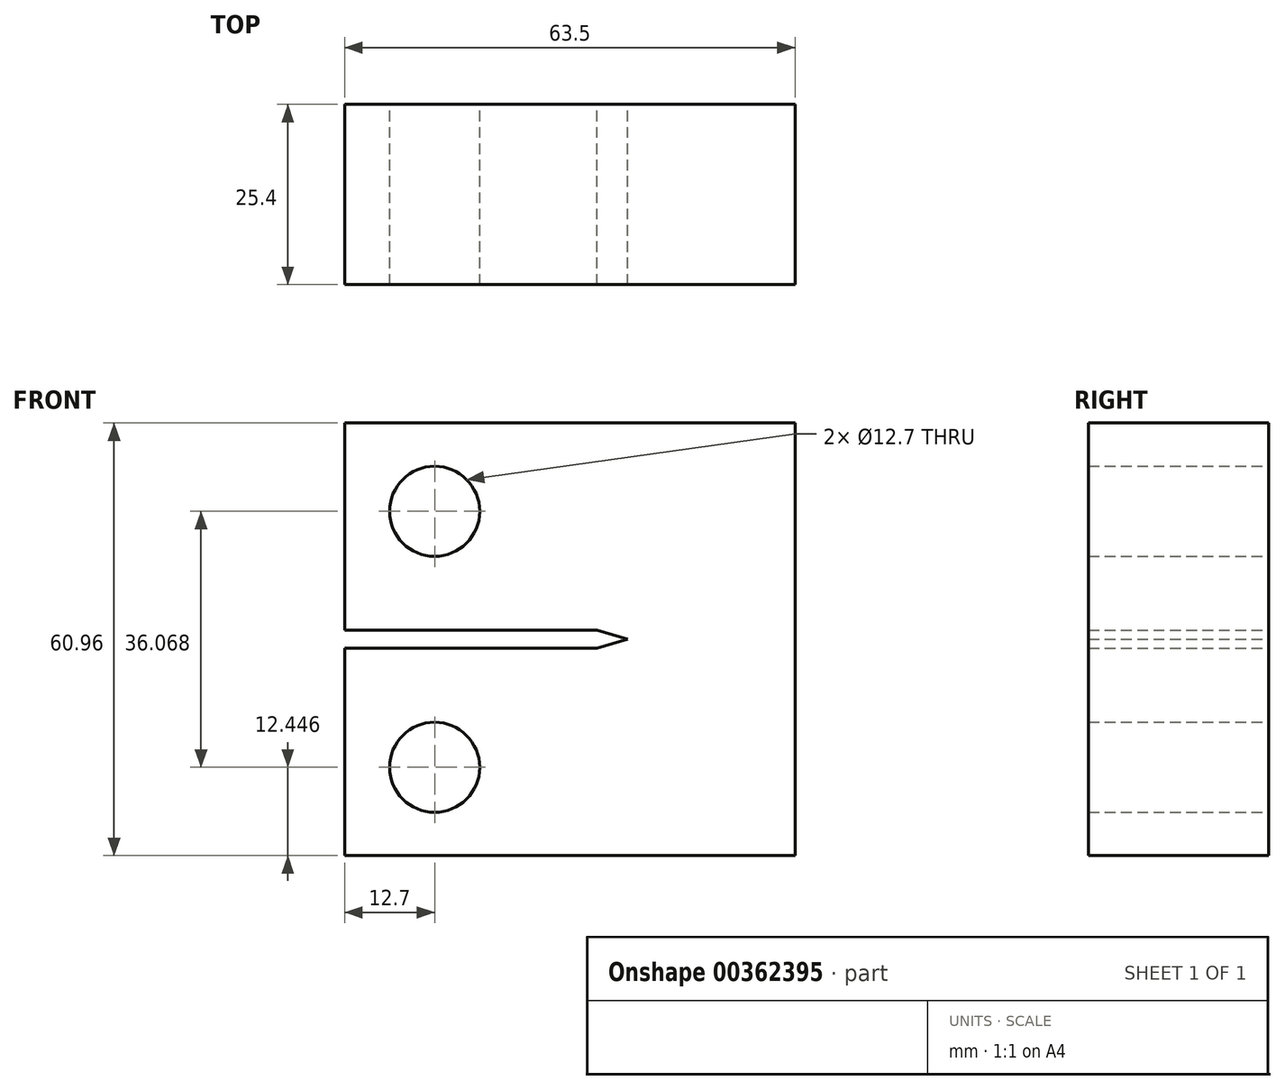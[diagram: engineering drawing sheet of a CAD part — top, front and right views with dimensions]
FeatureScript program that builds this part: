
annotation { "Feature Type Name" : "Feature", "Feature Type Description" : "" }
export const myFeature = defineFeature(function(context is Context, id is Id, definition is map)
    precondition{}
    {
        {
            var Q0;
            Q0=qCreatedBy(makeId("Front.planeOp"),FACE);
            var sketch = newSketch(context, id + "F0", { "sketchPlane" : qUnion([Q0])});
            skLineSegment(sketch, "E0.bottom", {"start": v(-31.75, -30.48) * mm, "end": v(31.75, -30.48) * mm});
            skLineSegment(sketch, "E0.top", {"start": v(-31.75, 30.48) * mm, "end": v(31.75, 30.48) * mm});
            skLineSegment(sketch, "E0.left", {"start": v(-31.75, -30.48) * mm, "end": v(-31.75, -1.27) * mm});
            skLineSegment(sketch, "E0.right", {"start": v(31.75, -30.48) * mm, "end": v(31.75, 30.48) * mm});
            skCircle(sketch, "E1", {"center": v(-19.05, 18.03) * mm, "radius": 6.35 * mm});
            skCircle(sketch, "E2", {"center": v(-19.05, -18.03) * mm, "radius": 6.35 * mm});
            skLineSegment(sketch, "E3.bottom", {"start": v(-31.75, -1.27) * mm, "end": v(3.81, -1.27) * mm});
            skLineSegment(sketch, "E3.top", {"start": v(-31.75, 1.27) * mm, "end": v(3.81, 1.27) * mm});
            skLineSegment(sketch, "E4", {"start": v(3.81, 1.27) * mm, "end": v(8.17, 0) * mm});
            skLineSegment(sketch, "E5", {"start": v(8.17, 0) * mm, "end": v(3.81, -1.27) * mm});
            skLineSegment(sketch, "E6.trimOffspring", {"start": v(-31.75, 1.27) * mm, "end": v(-31.75, 30.48) * mm});
            skSolve(sketch);
        }
        {
            var Q0;
            Q0 = qSketchRegion(id + "F0", true);
            extrude(context, id + "F1", {"entities" : qUnion([Q0]), "depth" : 25.4 * mm});
        }
    });
